# Revit family: floodlight_fl_21_iq_mini___pl64_5xa7772d4e2a_73bf
name_source: partatom
category: Lighting Fixtures
units: mm (PartAtom-declared; Revit-internal decimal feet)

## family parameters
Cut with Voids When Loaded = No
Host = Face
Light Source = No
Part Type = Normal
Room Calculation Point = No
Round Connector Dimension = Use Diameter
Shared = No

## types (1)
- --- (1 x LED, 17970 lm, 143 W, 4000K)
    Apparent Load = 143 VA
    CIE Flux Codes = 28 80 98 100 100
    Color Rendering = 70
    Color Temperature = 4000K
    Default Elevation = 1800 mm
    Description = Floodlight FL 21 iQ mini, floodlight, primary light control with lens, of PMMA, primary optical cover: protective disc, of toughened safety glass, transparent, light distribution: PL64, light emission: direct distribution, installation type: surface-mounted, lamps: LED, High Power LED, rated values: 17.970lm | 143W | 125,7lm/W (begin service life); end service life: 17.970lm | 151,6W; at 50% lumin. flux: 8.985lm | 60,8W | 147,8lm/W, colour temperature: 4000K, colour rendering: CRI > 70, light colour: 740, light setting 1 begin service life: 100% | 17.970lm | 143W | 125,7lm/W | 4.000K, light setting 1 end service life: 151,6W, further light settings possible, control: Street-Remote, Auto-Match, Temp-Guard, Night-Set, Smart-Wire, Desk-Remote (wireless, voltage-free reading and setting of iQ features in the workshop via application-optimized NFC function/RFID function), optimised constant luminous flux control (CLO 2.0), pre-setting: linear dimming characteristic, with terminal, 6-pole, mains connection: 220..240V, AC, 50/60Hz, luminaire housing, of diecast aluminium, powder-coated, SITECO metallic grey (DB 702S), corrosivity category C5 mid according to DIN EN ISO 12944, sealing non-destructively replaceable, design bracket, of diecast aluminium, powder-coated, SITECO metallic grey (DB 702S), protection rating (complete): IP66, insulation class (complete): insulation class II (safety insulation), certification: CE, ENEC, VDE, protection symbol: D, impact resistance: IK08, permissible operating ambient temperature: -40..+40°C, permissible operating ambient temperature for outdoor applications: -40..+50°C, standard: DIN EN 12944, LABS conformity tested according to VDMA 24364:2018-05, packaging unit: 1 piece

Light Distribution: PL64
    Height = 70 mm
    Lamp = 1 x LED
    Lamp Light Flux = 17970 lm
    Lamp Power = 143 W
    Lamp count = 1
    Length = 485 mm
    Luminous efficacy = 126 lm/W
    Manufacturer = Siteco
    ModVariant = No
    Model = 5XA7772D4E2A
    Mounting Place = Wall
    Mounting Type = Surface mounted
    Number of Poles = 1
    OnlyDefault = Yes
    Power Factor = 1
    Product Name = Floodlight FL 21 iQ mini | PL64
    Product group = floodlight | wall mounted
    ProductGroupID = 2002
    Protection Class = Protection class II
    Protection Degree = IP 66
    RLX_Detail_Level = 1
    RLX_Emergency_Light_Flux = 0 lm
    RLX_Emergency_Type = 0
    RLX_Emergency_Type_DB = No
    RlxData = <blob elided: 112409 chars, md5=401a9595>
    Socket = socket
    Standby Power = 0 W
    System Light Flux = 17970 lm
    System Power = 143 W
    Type Comments = factory setting: luminous flux: 100 % | dim-lin: 254 | 730 mA
    Type Image = l_1006634.jpg
    URL = http://relux.com
    VarID = @adj_165165
    Voltage = 0 V
    Weight = 0.00 kg
    Width = 337 mm

## geometry (parser evidence)
native form markers: Sweep x12
no freeform markers — native parametric forms only
